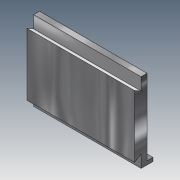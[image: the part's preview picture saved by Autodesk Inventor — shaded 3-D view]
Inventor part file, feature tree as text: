
AUTODESK INVENTOR PART (.ipt)
format: ipt  version: 2018.3 (Build 223284000, 284)  size: 143,872 bytes
history: native  units: in
note: dims shown in document units (in); Inventor stores cm internally (conversion verified against a paired STEP export)
features: extrude x4, sketch x4, mirror x1
ambient origin geometry x8: Origin, YZ Plane, XZ Plane, XY Plane, X Axis, Y Axis, Z Axis, Center Point
bodies: Solid1 (feature_tree)
feature tree (9):
  extrude  "Extrusion1"  Depth=0.24in
  extrude  "Extrusion2"  Depth=0.02in
  mirror  "Mirror1"
  extrude  "Extrusion4"  TaperAngle=60.0deg  [1 undecoded]
  extrude  "Extrusion5"  Depth=0.018in
  sketch  "Sketch1"  dims[d0=0.325in d1=0.24in]
  sketch  "Sketch2"  dims[d2=0.038in d3=0.0in d4=0.02in]
  sketch  "Sketch4"  dims[d5=0.0373in d6=60.0deg]
  sketch  "Sketch5"  dims[d7=0.325in d8=0.0in d15=0.0258in d16=0.0827in d17=0.096in d18=1.0in d19=0.0in d20=0.018in d21=0.218in d22=1.0in d23=0.0in]
note: 1 required parameter value undecoded (feature->parameter linkage not recoverable at this tier; creation-order binding heuristic only, values carry confidence <= 0.55)
